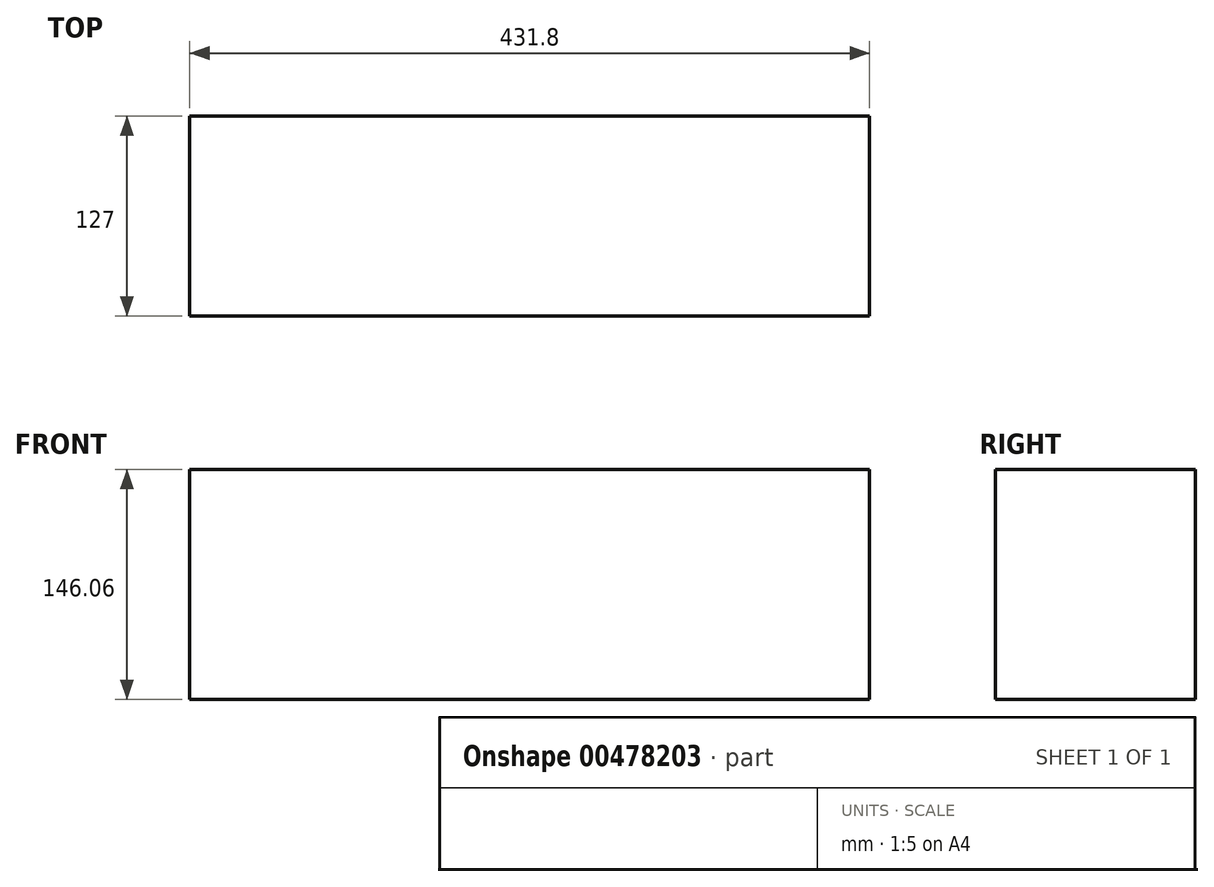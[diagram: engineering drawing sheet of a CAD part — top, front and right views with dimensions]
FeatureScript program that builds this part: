
annotation { "Feature Type Name" : "Feature", "Feature Type Description" : "" }
export const myFeature = defineFeature(function(context is Context, id is Id, definition is map)
    precondition{}
    {
        {
            var Q0;
            Q0=qCreatedBy(makeId("Front.planeOp"),FACE);
            var sketch = newSketch(context, id + "F0", { "sketchPlane" : qUnion([Q0])});
            skLineSegment(sketch, "E0.bottom", {"start": v(215.9, -73.02) * mm, "end": v(-215.9, -73.03) * mm});
            skLineSegment(sketch, "E0.top", {"start": v(215.9, 73.03) * mm, "end": v(-215.9, 73.02) * mm});
            skLineSegment(sketch, "E0.left", {"start": v(215.9, -73.02) * mm, "end": v(215.9, 73.03) * mm});
            skLineSegment(sketch, "E0.right", {"start": v(-215.9, -73.03) * mm, "end": v(-215.9, 73.03) * mm});
            skPoint(sketch, "E0.middle", {"position": v(0, 0) * mm});
            skSolve(sketch);
        }
        {
            var Q0;
            Q0=qSketchRegion(id+"F0",true);
            extrude(context, id + "F1", {"entities" : qUnion([Q0]), "depth" : 127 * mm});
        }
    });
